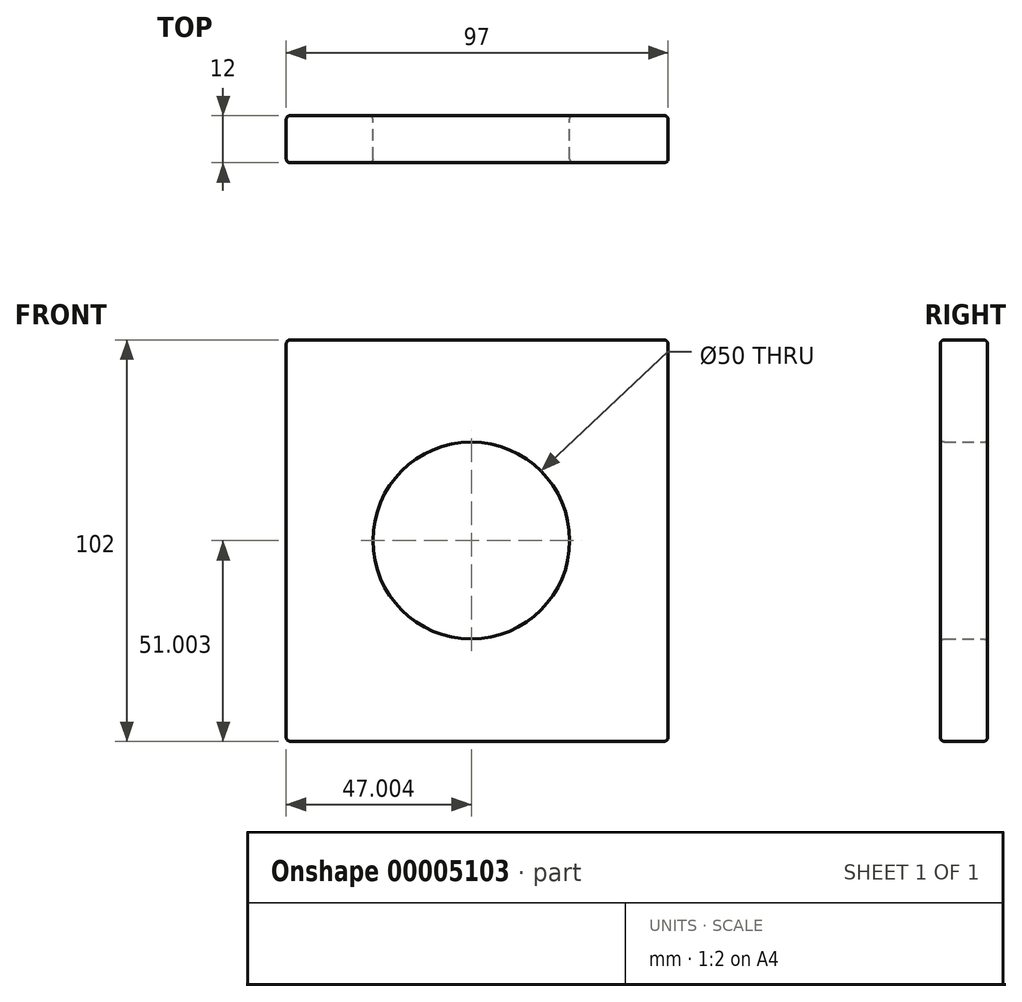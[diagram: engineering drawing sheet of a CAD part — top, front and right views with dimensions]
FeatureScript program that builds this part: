
annotation { "Feature Type Name" : "Feature", "Feature Type Description" : "" }
export const myFeature = defineFeature(function(context is Context, id is Id, definition is map)
    precondition{}
    {
        {
            var Q0;
            Q0=qCreatedBy(makeId("Front.planeOp"),FACE);
            var sketch = newSketch(context, id + "F0", { "sketchPlane" : qUnion([Q0])});
            skLineSegment(sketch, "E0.bottom", {"start": v(-85.8, 86.97) * mm, "end": v(11.2, 86.97) * mm});
            skLineSegment(sketch, "E0.top", {"start": v(-85.8, -15.03) * mm, "end": v(11.2, -15.03) * mm});
            skLineSegment(sketch, "E0.left", {"start": v(-85.8, 86.97) * mm, "end": v(-85.8, -15.03) * mm});
            skLineSegment(sketch, "E0.right", {"start": v(11.2, 86.97) * mm, "end": v(11.2, -15.03) * mm});
            skCircle(sketch, "E1", {"center": v(-38.8, 35.97) * mm, "radius": 25 * mm});
            skSolve(sketch);
        }
        {
            var Q0;
            Q0=makeQuery(id+"F0.imprint","IMPRINT",FACE,{"disambiguationData":[TD([[makeQuery(id+"F0.imprint","IMPRINT",EDGE,{"derivedFrom":sQuery(id+"F0.wireOp",EDGE,"E0.bottom")}),-1.0]])]});
            extrude(context, id + "F1", {"entities" : qUnion([Q0]), "depth" : 12 * mm});
        }
        {
            var Q0;
            Q0=makeQuery(id+"F1.opExtrude","SWEPT_EDGE",EDGE,{"disambiguationData":[OSD([sQuery(id+"F0.wireOp",EDGE,"E0.bottom"),sQuery(id+"F0.wireOp",EDGE,"E0.right")])]});
            var Q1;
            Q1=makeQuery(id+"F1.opExtrude","SWEPT_EDGE",EDGE,{"disambiguationData":[OSD([sQuery(id+"F0.wireOp",EDGE,"E0.top"),sQuery(id+"F0.wireOp",EDGE,"E0.right")])]});
            var Q2;
            Q2=makeQuery(id+"F1.opExtrude","SWEPT_EDGE",EDGE,{"disambiguationData":[OSD([sQuery(id+"F0.wireOp",EDGE,"E0.bottom"),sQuery(id+"F0.wireOp",EDGE,"E0.left")])]});
            var Q3;
            Q3=makeQuery(id+"F1.opExtrude","SWEPT_EDGE",EDGE,{"disambiguationData":[OSD([sQuery(id+"F0.wireOp",EDGE,"E0.top"),sQuery(id+"F0.wireOp",EDGE,"E0.left")])]});
            var Q4;
            Q4=makeQuery(id+"F1.opExtrude","CAP_EDGE",EDGE,{"disambiguationData":[OSD([sQuery(id+"F0.wireOp",EDGE,"E0.bottom")])],"isStart":false});
            var Q5;
            Q5=makeQuery(id+"F1.opExtrude","CAP_EDGE",EDGE,{"disambiguationData":[OSD([sQuery(id+"F0.wireOp",EDGE,"E0.left")])],"isStart":false});
            var Q6;
            Q6=makeQuery(id+"F1.opExtrude","CAP_EDGE",EDGE,{"disambiguationData":[OSD([sQuery(id+"F0.wireOp",EDGE,"E0.top")])],"isStart":false});
            var Q7;
            Q7=makeQuery(id+"F1.opExtrude","CAP_EDGE",EDGE,{"disambiguationData":[OSD([sQuery(id+"F0.wireOp",EDGE,"E0.right")])],"isStart":false});
            var Q8;
            Q8=makeQuery(id+"F1.opExtrude","CAP_EDGE",EDGE,{"disambiguationData":[OSD([sQuery(id+"F0.wireOp",EDGE,"E1")])],"isStart":false});
            var Q9;
            Q9=makeQuery(id+"F1.opExtrude","CAP_EDGE",EDGE,{"disambiguationData":[OSD([sQuery(id+"F0.wireOp",EDGE,"E0.left")])],"isStart":true});
            var Q10;
            Q10=makeQuery(id+"F1.opExtrude","CAP_EDGE",EDGE,{"disambiguationData":[OSD([sQuery(id+"F0.wireOp",EDGE,"E0.bottom")])],"isStart":true});
            var Q11;
            Q11=makeQuery(id+"F1.opExtrude","CAP_EDGE",EDGE,{"disambiguationData":[OSD([sQuery(id+"F0.wireOp",EDGE,"E0.top")])],"isStart":true});
            var Q12;
            Q12=makeQuery(id+"F1.opExtrude","CAP_EDGE",EDGE,{"disambiguationData":[OSD([sQuery(id+"F0.wireOp",EDGE,"E0.right")])],"isStart":true});
            var Q13;
            Q13=makeQuery(id+"F1.opExtrude","CAP_EDGE",EDGE,{"disambiguationData":[OSD([sQuery(id+"F0.wireOp",EDGE,"E1")])],"isStart":true});
            fillet(context, id + "F2", {"entities" : qUnion([Q0, Q1, Q2, Q3, Q4, Q5, Q6, Q7, Q8, Q9, Q10, Q11, Q12, Q13]), "radius" : 1 * mm, "tangentPropagation" : true, "allowEdgeOverflow" : false});
        }
    });
